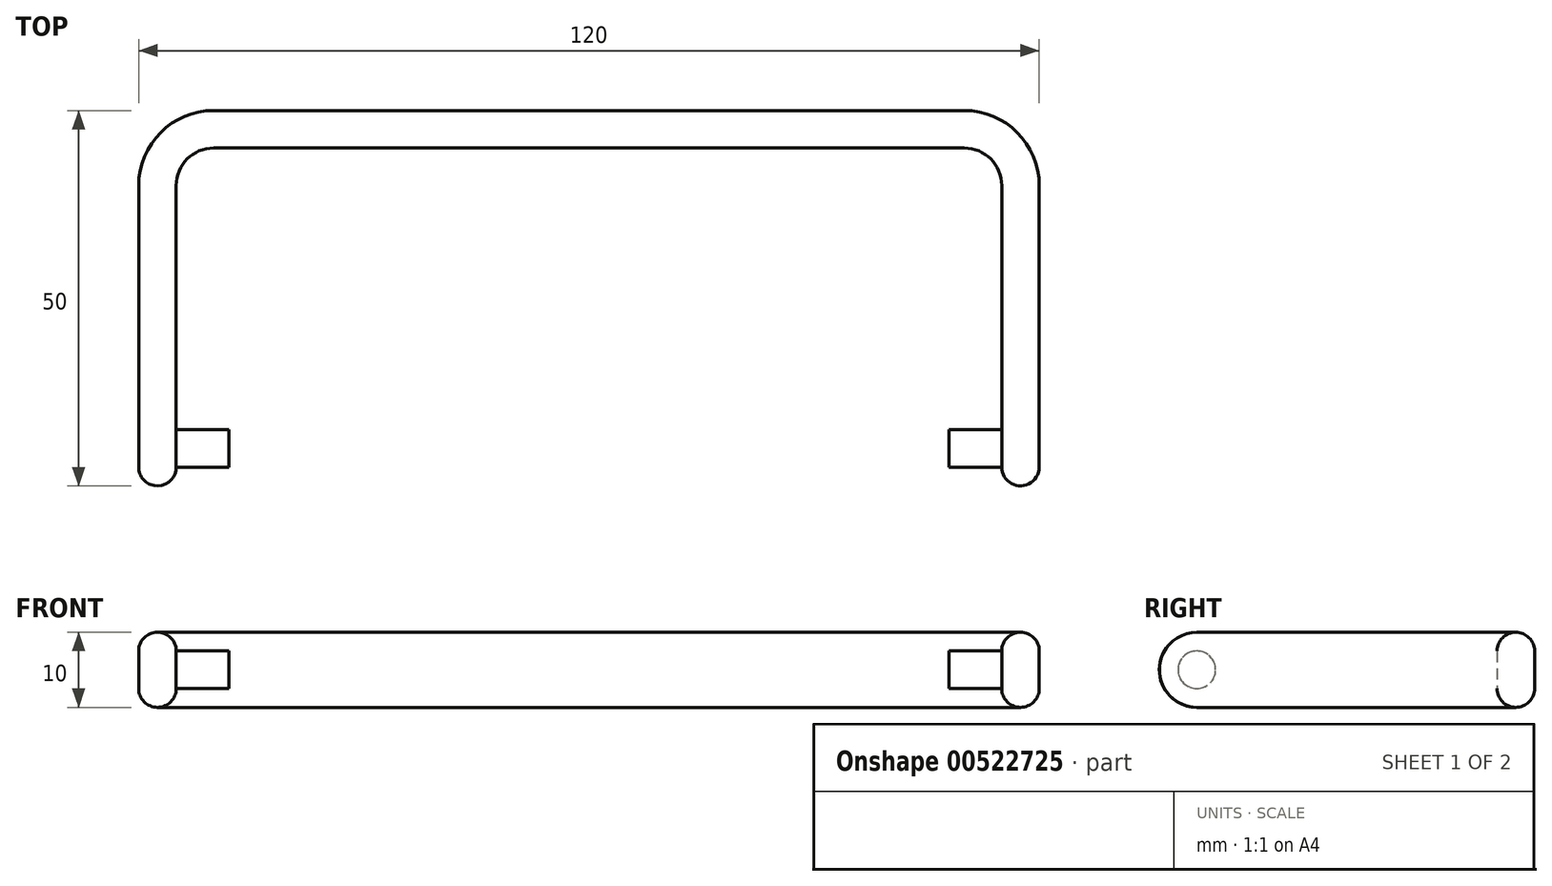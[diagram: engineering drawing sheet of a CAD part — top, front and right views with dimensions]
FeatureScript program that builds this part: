
annotation { "Feature Type Name" : "Feature", "Feature Type Description" : "" }
export const myFeature = defineFeature(function(context is Context, id is Id, definition is map)
    precondition{}
    {
        {
            var Q0;
            Q0=qCreatedBy(makeId("Top.planeOp"),FACE);
            var sketch = newSketch(context, id + "F0", { "sketchPlane" : qUnion([Q0])});
            skLineSegment(sketch, "E0", {"start": v(-55, 0) * mm, "end": v(-55, 40) * mm});
            skLineSegment(sketch, "E1", {"start": v(-50, 45) * mm, "end": v(50, 45) * mm});
            skLineSegment(sketch, "E2", {"start": v(55, 40) * mm, "end": v(55, 0) * mm});
            skLineSegment(sketch, "E3", {"start": v(0, -81.82) * mm, "end": v(0, 107.27) * mm, "construction": true});
            skLineSegment(sketch, "E4.0", {"start": v(60, 40) * mm, "end": v(60, 0) * mm});
            skLineSegment(sketch, "E4.1", {"start": v(-50, 50) * mm, "end": v(50, 50) * mm});
            skLineSegment(sketch, "E4.2", {"start": v(-60, 0) * mm, "end": v(-60, 40) * mm});
            skPoint(sketch, "E5.visualSharp", {"position": v(-55, 45) * mm});
            skArc(sketch, "E5.filletArc", {"start": v(-50, 45) * mm, "mid": v(-53.54, 43.54) * mm, "end": v(-55, 40) * mm});
            skPoint(sketch, "E6.visualSharp", {"position": v(-60, 50) * mm});
            skArc(sketch, "E6.filletArc", {"start": v(-50, 50) * mm, "mid": v(-57.07, 47.07) * mm, "end": v(-60, 40) * mm});
            skPoint(sketch, "E7.visualSharp", {"position": v(60, 50) * mm});
            skArc(sketch, "E7.filletArc", {"start": v(60, 40) * mm, "mid": v(57.07, 47.07) * mm, "end": v(50, 50) * mm});
            skPoint(sketch, "E8.visualSharp", {"position": v(55, 45) * mm});
            skArc(sketch, "E8.filletArc", {"start": v(55, 40) * mm, "mid": v(53.54, 43.54) * mm, "end": v(50, 45) * mm});
            skLineSegment(sketch, "E9", {"start": v(-60, 0) * mm, "end": v(-55, 0) * mm});
            skLineSegment(sketch, "E10", {"start": v(55, 0) * mm, "end": v(60, 0) * mm});
            skSolve(sketch);
        }
        {
            var Q0;
            Q0=makeQuery(id+"F0.imprint","IMPRINT",FACE,{"disambiguationData":[TD([[makeQuery(id+"F0.imprint","IMPRINT",EDGE,{"derivedFrom":sQuery(id+"F0.wireOp",EDGE,"E0")}),1.0]])]});
            extrude(context, id + "F1", {"entities" : qUnion([Q0]), "depth" : 10 * mm, "offsetDistance" : 25 * mm});
        }
        {
            var Q0;
            Q0=makeQuery(id+"F1.opExtrude","CAP_EDGE",EDGE,{"disambiguationData":[OSD([sQuery(id+"F0.wireOp",EDGE,"E9")])],"isStart":false});
            var Q1;
            Q1=makeQuery(id+"F1.opExtrude","CAP_EDGE",EDGE,{"disambiguationData":[OSD([sQuery(id+"F0.wireOp",EDGE,"E9")])],"isStart":true});
            var Q2;
            Q2=makeQuery(id+"F1.opExtrude","CAP_EDGE",EDGE,{"disambiguationData":[OSD([sQuery(id+"F0.wireOp",EDGE,"E10")])],"isStart":true});
            var Q3;
            Q3=makeQuery(id+"F1.opExtrude","CAP_EDGE",EDGE,{"disambiguationData":[OSD([sQuery(id+"F0.wireOp",EDGE,"E10")])],"isStart":false});
            fillet(context, id + "F2", {"entities" : qUnion([Q0, Q1, Q2, Q3]), "radius" : 5 * mm, "tangentPropagation" : true, "allowEdgeOverflow" : false});
        }
        {
            var Q0;
            Q0=makeQuery(id+"F1.opExtrude","CAP_EDGE",EDGE,{"disambiguationData":[OSD([sQuery(id+"F0.wireOp",EDGE,"E4.0")])],"isStart":false});
            var Q1;
            Q1=makeQuery(id+"F1.opExtrude","CAP_EDGE",EDGE,{"disambiguationData":[OSD([sQuery(id+"F0.wireOp",EDGE,"E2")])],"isStart":false});
            fillet(context, id + "F3", {"entities" : qUnion([Q0, Q1]), "radius" : 2.5 * mm, "tangentPropagation" : true, "allowEdgeOverflow" : false});
        }
        {
            var Q0;
            Q0=makeQuery(id+"F1.opExtrude","SWEPT_FACE",FACE,{"disambiguationData":[OSD([sQuery(id+"F0.wireOp",EDGE,"E0")])]});
            var sketch = newSketch(context, id + "F4", { "sketchPlane" : qUnion([Q0])});
            skLineSegment(sketch, "E11", {"start": v(5, 7.5) * mm, "end": v(5, 2.5) * mm, "construction": true});
            skLineSegment(sketch, "E12", {"start": v(2.5, 5) * mm, "end": v(8.96, 5) * mm, "construction": true});
            skPoint(sketch, "E13", {"position": v(2.5, 5) * mm});
            skCircle(sketch, "E14", {"center": v(5, 5) * mm, "radius": 2.5 * mm});
            skSolve(sketch);
        }
        {
            var Q0;
            Q0=makeQuery(id+"F4.imprint","IMPRINT",FACE,{"disambiguationData":[TD([[makeQuery(id+"F4.imprint","IMPRINT",EDGE,{"derivedFrom":sQuery(id+"F4.wireOp",EDGE,"E14")}),1.0]])]});
            extrude(context, id + "F5", {"entities" : qUnion([Q0]), "operationType" : NewBodyOperationType.ADD, "depth" : 7 * mm, "offsetDistance" : 25 * mm});
        }
        {
            var Q0;
            Q0=makeQuery(id+"F1.opExtrude","SWEPT_FACE",FACE,{"disambiguationData":[OSD([sQuery(id+"F0.wireOp",EDGE,"E2")])]});
            var sketch = newSketch(context, id + "F6", { "sketchPlane" : qUnion([Q0])});
            skCircle(sketch, "E15.0", {"center": v(-5, 5) * mm, "radius": 2.5 * mm});
            skSolve(sketch);
        }
        {
            var Q0;
            Q0=makeQuery(id+"F6.imprint","IMPRINT",FACE,{"disambiguationData":[TD([[makeQuery(id+"F6.imprint","IMPRINT",EDGE,{"derivedFrom":sQuery(id+"F6.wireOp",EDGE,"E15.0")}),1.0]])]});
            extrude(context, id + "F7", {"entities" : qUnion([Q0]), "operationType" : NewBodyOperationType.ADD, "depth" : 7 * mm, "offsetDistance" : 25 * mm});
        }
    });
